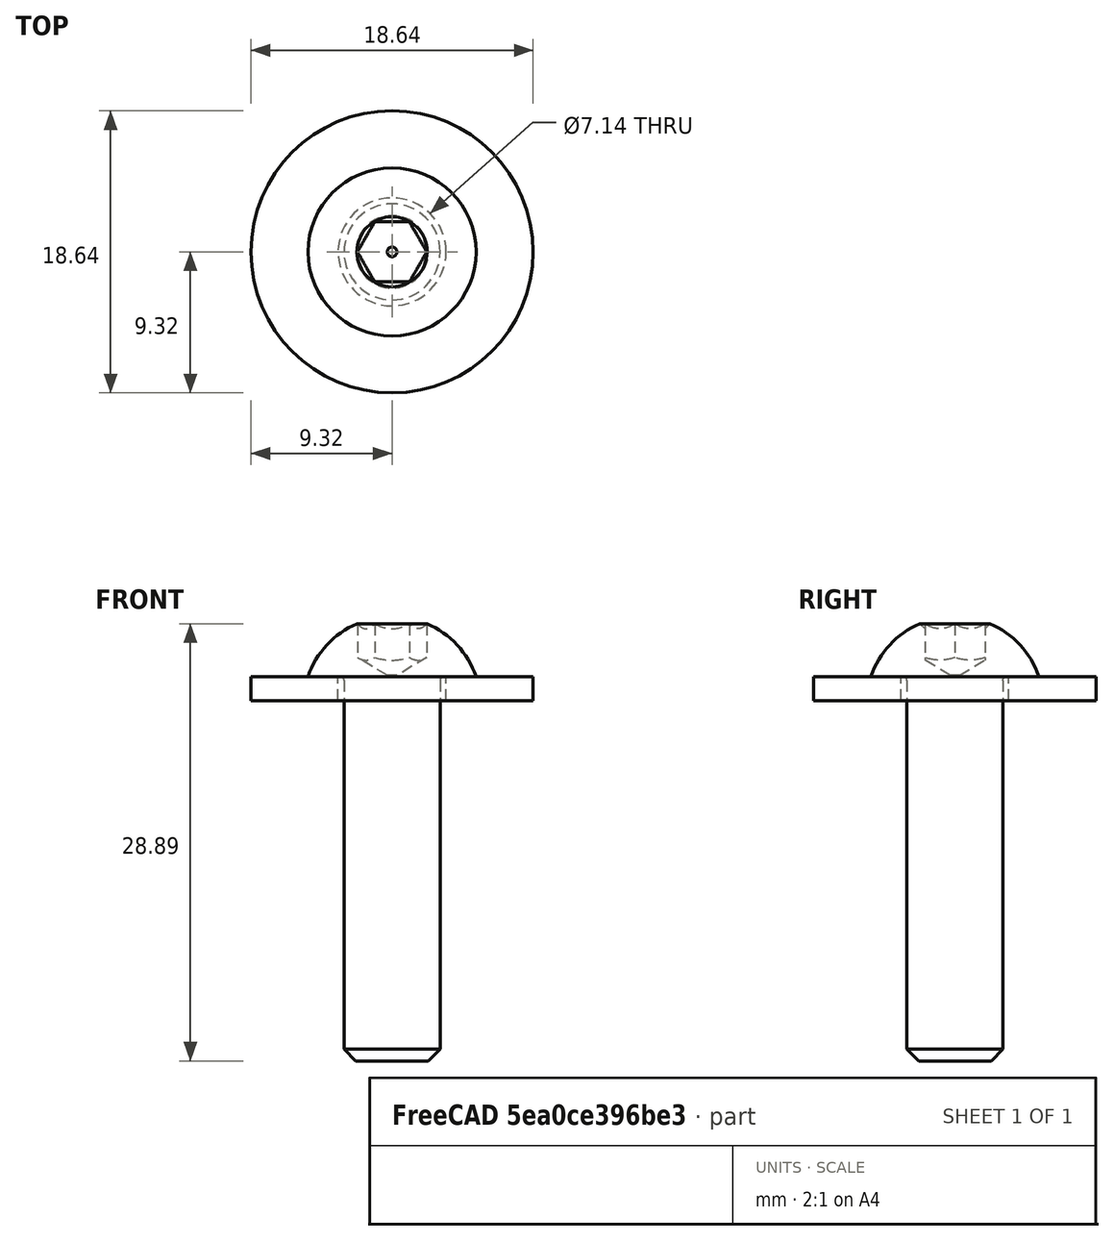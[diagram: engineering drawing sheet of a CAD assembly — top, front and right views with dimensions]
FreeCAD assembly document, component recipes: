
FREECAD ASSEMBLY — COMPONENT RECIPES ("Y-axis")

This assembly document has 3 components, labeled P0..P2 below (a component is one placed body or linked part). 0 of them carry a construction recipe — the FreeCAD feature program that regenerates the part from scratch, quoted from this document or its linked companion documents; the rest are supplied as boundary geometry only. No exploded tour is included for this assembly.
COMPONENT P0 — geometry summary ("Link(Y-beam 2x4)"; no construction recipe available for this part):
  bounding box: 830.0 x 101.6 x 50.8 mm
  tessellated surface: 16,844 triangles
  volume: 1221944 mm^3 (29% of its bounding box)
  symmetry: 2-fold rotationally symmetric about the x axis; 2-fold rotationally symmetric about the y axis; 2-fold rotationally symmetric about the z axis; mirror-symmetric across its x mid-plane, y mid-plane, z mid-plane
COMPONENT P1 — geometry summary ("Link001(Cross member 2x2)"; no construction recipe available for this part):
  bounding box: 448.0 x 50.8 x 50.8 mm
  tessellated surface: 3,200 triangles
  volume: 364233 mm^3 (32% of its bounding box)
  symmetry: 4-fold rotationally symmetric about the x axis; 2-fold rotationally symmetric about the y axis; 2-fold rotationally symmetric about the z axis; mirror-symmetric across its x mid-plane, y mid-plane, z mid-plane
COMPONENT P2 — geometry summary ("Link008(Y-beam 2x4)"; no construction recipe available for this part):
  bounding box: 830.0 x 101.6 x 50.8 mm
  tessellated surface: 16,844 triangles
  volume: 1221944 mm^3 (29% of its bounding box)
  symmetry: 2-fold rotationally symmetric about the x axis; 2-fold rotationally symmetric about the y axis; 2-fold rotationally symmetric about the z axis; mirror-symmetric across its x mid-plane, y mid-plane, z mid-plane
PROVENANCE & LICENSES
A FreeCAD (.FCStd) document from a public repository crawl; recipes are the document's own serialized feature recipes (and, for linked parts, companion documents' recipes).
License: mit.
